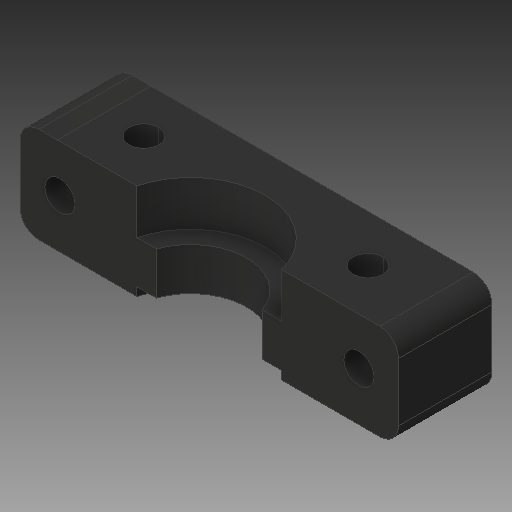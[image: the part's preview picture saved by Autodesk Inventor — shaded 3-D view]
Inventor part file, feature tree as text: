
AUTODESK INVENTOR PART (.ipt)
format: ipt  version: 2018 (Build 220112000, 112)  size: 202,240 bytes
history: native  units: mm
features: sketch x9, other x3
ambient origin geometry x8: Origin, YZ Plane, XZ Plane, XY Plane, X Axis, Y Axis, Z Axis, Center Point
bodies: Solid1 (feature_tree)
feature tree (12):
  other  "Hotend Clamp P2_MIR.ipt"
  other  "Solid1::Hotend Clamp P2_MIR.ipt"
  other  "TaggingFeature1"
  sketch  "Sketch1"  dims[d0=10.0mm]
  sketch  "Sketch2"
  sketch  "Sketch3"
  sketch  "Sketch4"
  sketch  "Sketch5"
  sketch  "Sketch6"
  sketch  "Sketch7"
  sketch  "Sketch8"
  sketch  "Sketch9"
